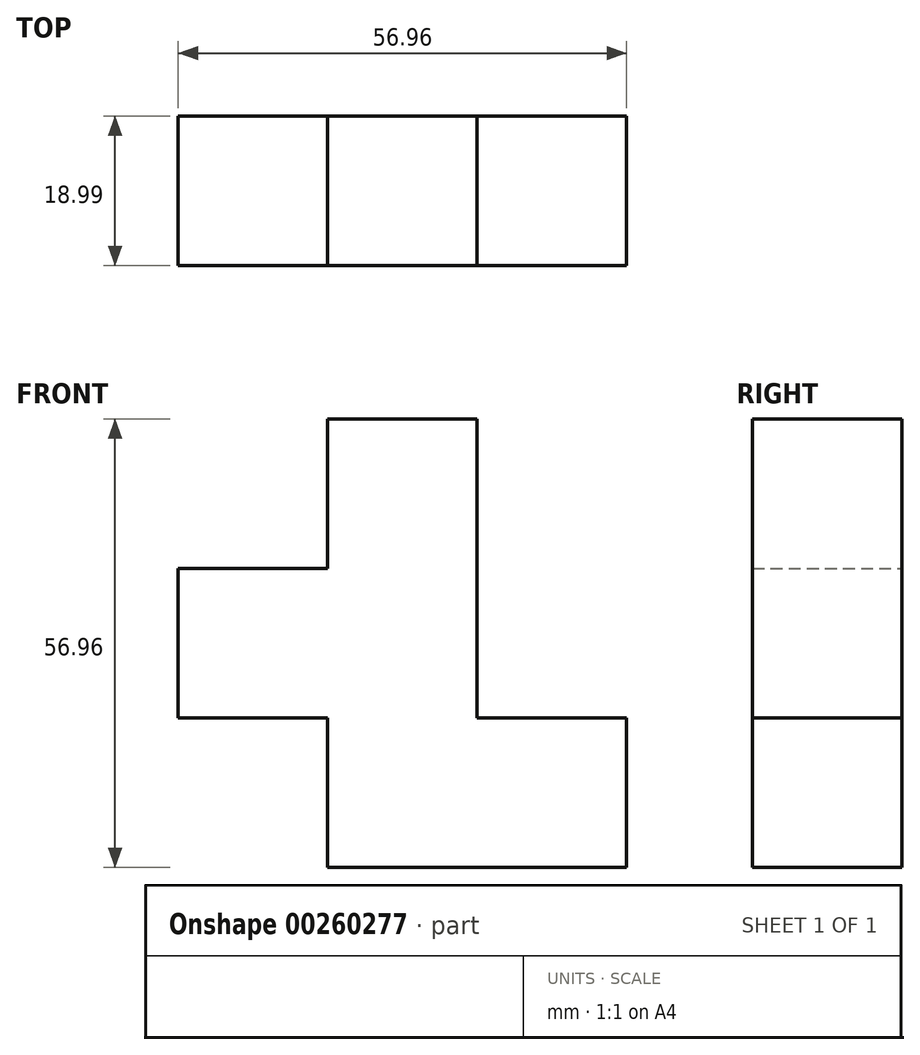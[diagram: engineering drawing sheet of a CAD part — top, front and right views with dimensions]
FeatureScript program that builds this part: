
annotation { "Feature Type Name" : "Feature", "Feature Type Description" : "" }
export const myFeature = defineFeature(function(context is Context, id is Id, definition is map)
    precondition{}
    {
        {
            var Q0;
            Q0=qCreatedBy(makeId("Front.planeOp"),FACE);
            var sketch = newSketch(context, id + "F0", { "sketchPlane" : qUnion([Q0])});
            skLineSegment(sketch, "E0.bottom", {"start": v(0, 0) * mm, "end": v(-18.99, 0) * mm});
            skLineSegment(sketch, "E0.top", {"start": v(0, 18.99) * mm, "end": v(-18.99, 18.99) * mm});
            skLineSegment(sketch, "E0.left", {"start": v(0, 0) * mm, "end": v(0, 18.99) * mm});
            skLineSegment(sketch, "E0.right", {"start": v(-18.99, 0) * mm, "end": v(-18.99, 18.99) * mm});
            skLineSegment(sketch, "E1.bottom", {"start": v(-18.99, 18.99) * mm, "end": v(0, 18.99) * mm});
            skLineSegment(sketch, "E2.bottom", {"start": v(-18.99, 0) * mm, "end": v(0, 0) * mm});
            skLineSegment(sketch, "E2.top", {"start": v(-18.99, -18.99) * mm, "end": v(0, -18.99) * mm});
            skLineSegment(sketch, "E2.left", {"start": v(-18.99, 0) * mm, "end": v(-18.99, -18.99) * mm});
            skLineSegment(sketch, "E2.right", {"start": v(0, 0) * mm, "end": v(0, -18.99) * mm});
            skLineSegment(sketch, "E3.top", {"start": v(-18.99, -37.97) * mm, "end": v(0, -37.97) * mm});
            skLineSegment(sketch, "E3.left", {"start": v(-18.99, -18.99) * mm, "end": v(-18.99, -37.97) * mm});
            skLineSegment(sketch, "E3.right", {"start": v(0, -18.99) * mm, "end": v(0, -37.97) * mm});
            skLineSegment(sketch, "E4.bottom", {"start": v(0, -18.99) * mm, "end": v(18.99, -18.99) * mm});
            skLineSegment(sketch, "E4.top", {"start": v(0, -37.97) * mm, "end": v(18.99, -37.97) * mm});
            skLineSegment(sketch, "E4.right", {"start": v(18.99, -18.99) * mm, "end": v(18.99, -37.97) * mm});
            skLineSegment(sketch, "E5.bottom", {"start": v(-18.99, 0) * mm, "end": v(-37.97, 0) * mm});
            skLineSegment(sketch, "E5.top", {"start": v(-18.99, -18.99) * mm, "end": v(-37.97, -18.99) * mm});
            skLineSegment(sketch, "E5.right", {"start": v(-37.97, 0) * mm, "end": v(-37.97, -18.99) * mm});
            skPoint(sketch, "E1.right.end.orphan", {"position": v(0, 37.97) * mm});
            skSolve(sketch);
        }
        {
            var Q0;
            Q0 = qSketchRegion(id + "F0", true);
            extrude(context, id + "F1", {"entities" : qUnion([Q0]), "depth" : 18.99 * mm});
        }
    });
